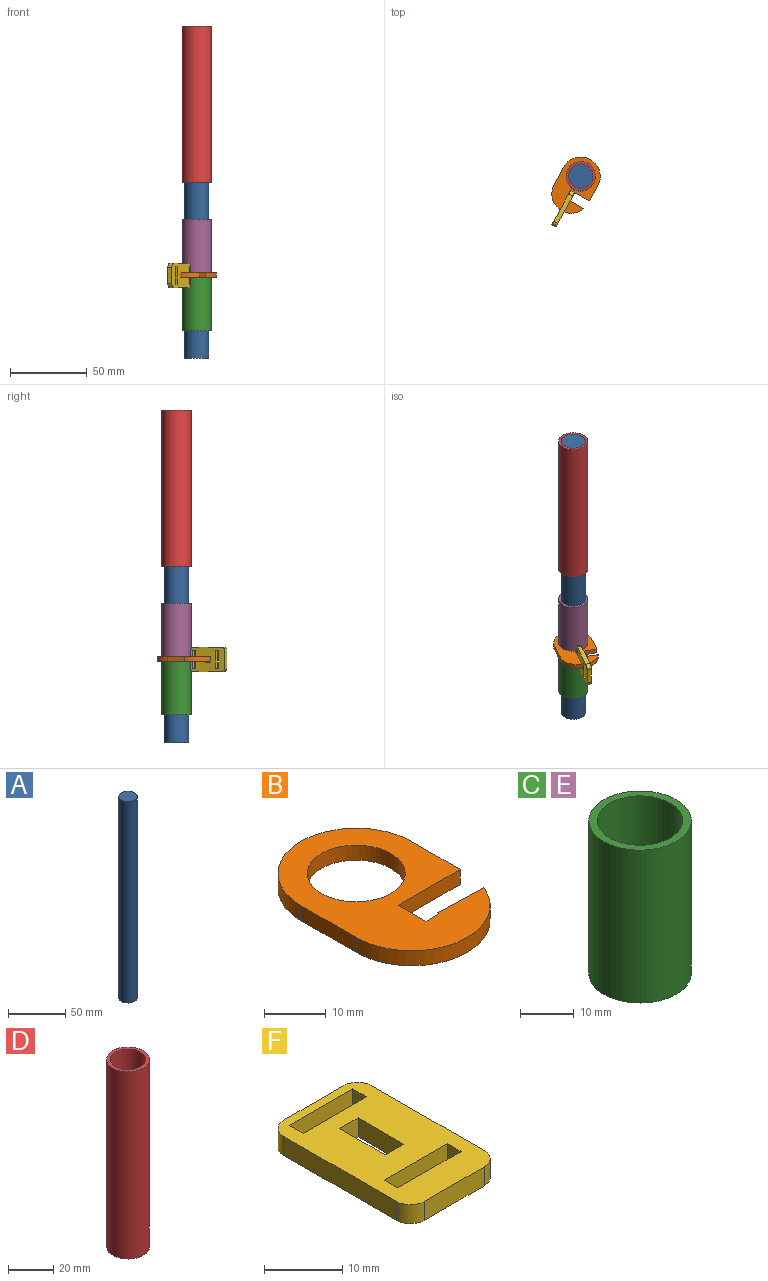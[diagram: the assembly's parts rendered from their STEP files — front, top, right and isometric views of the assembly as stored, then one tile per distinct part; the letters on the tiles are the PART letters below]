
ASSEMBLY  parts=6 mates=9
PART A: 3 faces, bbox 15.9x15.9x215.9 mm
  f0: cylinder r=7.94mm len=215.9mm, axis (0,0,-1), area 10767.5mm2, adj f1,f2
  f1: plane 15.88x15.88mm, normal (0,0,1), area 197.9mm2, adj f0
  f2: plane 15.88x15.88mm, normal (0,0,-1), area 197.9mm2, adj f0
PART B: 12 faces, bbox 25.4x38.1x3 mm
  f0: cylinder r=12.7mm len=24.47mm, axis (0,0,1), area 104.1mm2, adj f1,f3,f6,f9
  f1: plane 38.1x25.4mm, normal (0,0,1), area 544.4mm2, adj f0,f2,f3,f4,f5,f7,f8,f9
  f2: cylinder r=12.7mm len=25.4mm, axis (0,0,1), area 118.6mm2, adj f1,f3,f5,f6
  f3: plane 12.7x2.97mm, normal (-1,0,0), area 37.7mm2, adj f0,f1,f2,f6
  f4: cylinder r=7.94mm len=15.88mm, axis (0,0,1), area 148.2mm2, adj f1,f6
  f5: plane 11.11x2.97mm, normal (1,0,0), area 33mm2, adj f1,f2,f6,f7
  f6: plane 38.1x25.4mm, normal (0,0,-1), area 544.4mm2, adj f0,f2,f3,f4,f5,f7,f8,f9
  f7: plane 14.19x2.97mm, normal (0,-1,0), area 42.2mm2, adj f1,f5,f6,f8
  f8: plane 6.35x2.97mm, normal (1,0,0), area 18.9mm2, adj f1,f6,f7,f10
  f9: plane 10.29x2.97mm, normal (0.03,1,0), area 30.6mm2, adj f0,f1,f6,f11
  f10: plane 2.97x2.97mm, normal (0,1,0), area 8.8mm2, adj f1,f6,f8,f11
  f11: plane 2.97x0.32mm, normal (-1,0,0), area 0.9mm2, adj f1,f6,f9,f10
PART C: 4 faces, bbox 19.1x19.1x34.8 mm
  f0: cylinder r=7.94mm len=34.77mm, axis (0,0,-1), area 1734.2mm2, adj f2,f3
  f1: cylinder r=9.53mm len=34.77mm, axis (0,0,-1), area 2081mm2, adj f2,f3
  f2: plane 19.05x19.05mm, normal (0,0,1), area 87.1mm2, adj f0,f1
  f3: plane 19.05x19.05mm, normal (0,0,-1), area 87.1mm2, adj f0,f1
PART D: 4 faces, bbox 19.1x19.1x101.6 mm
  f0: cylinder r=7.94mm len=101.6mm, axis (0,0,-1), area 5067.1mm2, adj f2,f3
  f1: cylinder r=9.53mm len=101.6mm, axis (0,0,-1), area 6080.5mm2, adj f2,f3
  f2: plane 19.05x19.05mm, normal (0,0,1), area 87.1mm2, adj f0,f1
  f3: plane 19.05x19.05mm, normal (0,0,-1), area 87.1mm2, adj f0,f1
PART E: same geometry as C
PART F: 22 faces, bbox 15.9x25.4x3 mm
  f0: plane 25.4x15.88mm, normal (0,0,-1), area 313.1mm2, adj f2,f3,f4,f5,f6,f7,f8,f9
  f1: plane 25.4x15.88mm, normal (0,0,1), area 313.1mm2, adj f2,f3,f4,f5,f6,f7,f8,f9
  f2: cylinder r=2.54mm len=2.97mm, axis (0,0,1), area 11.9mm2, adj f0,f1,f3,f9
  f3: plane 10.8x2.97mm, normal (0,-1,0), area 32.1mm2, adj f0,f1,f2,f4
  f4: cylinder r=2.54mm len=2.97mm, axis (0,0,1), area 11.9mm2, adj f0,f1,f3,f5
  f5: plane 20.32x2.97mm, normal (1,0,0), area 60.4mm2, adj f0,f1,f4,f6
  f6: cylinder r=2.54mm len=2.97mm, axis (0,0,1), area 11.9mm2, adj f0,f1,f5,f7
  f7: plane 10.8x2.97mm, normal (0,1,0), area 32.1mm2, adj f0,f1,f6,f8
  f8: cylinder r=2.54mm len=2.97mm, axis (0,0,1), area 11.9mm2, adj f0,f1,f7,f9
  f9: plane 20.32x2.97mm, normal (-1,0,0), area 60.4mm2, adj f0,f1,f2,f8
  f10: plane 3.35x2.97mm, normal (0,1,0), area 10mm2, adj f0,f1,f11,f12
  f11: plane 8.26x2.97mm, normal (1,0,0), area 24.5mm2, adj f0,f1,f10,f13
  f12: plane 8.26x2.97mm, normal (-1,0,0), area 24.5mm2, adj f0,f1,f10,f13
  f13: plane 3.35x2.97mm, normal (0,-1,0), area 10mm2, adj f0,f1,f11,f12
  f14: plane 11.43x2.97mm, normal (0,1,0), area 34mm2, adj f0,f1,f15,f16
  f15: plane 2.97x2.49mm, normal (1,0,0), area 7.4mm2, adj f0,f1,f14,f17
  f16: plane 2.97x2.49mm, normal (-1,0,0), area 7.4mm2, adj f0,f1,f14,f17
  f17: plane 11.43x2.97mm, normal (0,-1,0), area 34mm2, adj f0,f1,f15,f16
  f18: plane 11.43x2.97mm, normal (0,-1,0), area 34mm2, adj f0,f1,f19,f21
  f19: plane 2.97x2.49mm, normal (1,0,0), area 7.4mm2, adj f0,f1,f18,f20
  f20: plane 11.43x2.97mm, normal (0,1,0), area 34mm2, adj f0,f1,f19,f21
  f21: plane 2.97x2.49mm, normal (-1,0,0), area 7.4mm2, adj f0,f1,f18,f20
PLACE A t=(-34.37,58.25,10.11)mm fixed
PLACE B rot(axis=(0,0,-1),28.5deg) t=(-34.37,58.86,65.48)mm
PLACE C rot(axis=(0,0,1),123.7deg) t=(-34.37,58.86,27.73)mm
PLACE D t=(-34.37,58.86,124.41)mm
PLACE E t=(-34.37,58.86,65.48)mm
PLACE F rot(axis=(0.24,0.94,-0.24),93.5deg) t=(-32.94,58.38,63.04)mm
MATE cylindrical D.f0 <-> A.f0  axis (0,0,-1) through (-34.37,58.86,226.01)mm
MATE cylindrical E.f0 <-> A.f0  axis (0,0,-1) through (-34.37,58.86,82.87)mm
MATE planar B.f6 <-> C.f0  axis (0,0,-1) through (-38.67,52.77,62.51)mm
MATE cylindrical B.f2 <-> A.f0  axis (0,0,1) through (-34.37,58.86,63.99)mm
MATE planar F.f0 <-> B.f8  axis (-0.88,0.48,0) through (-44,44.22,63.8)mm
MATE planar F.f13 <-> B.f10  axis (-0.48,-0.88,0) through (-42.69,43.51,63.8)mm
MATE planar B.f2 <-> E.f0  axis (0,0,1) through (-34.37,58.86,65.48)mm
MATE cylindrical C.f0 <-> A.f0  axis (0,0,-1) through (-34.37,58.86,27.73)mm
MATE planar F.f11 <-> B.f1  axis (0,0,-1) through (-44.66,39.88,65.48)mm
